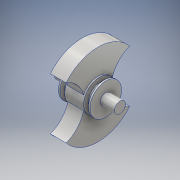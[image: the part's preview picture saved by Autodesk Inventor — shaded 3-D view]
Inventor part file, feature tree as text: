
AUTODESK INVENTOR PART (.ipt)
format: ipt  version: 2016 (Build 200138000, 138)  size: 163,328 bytes
history: native  units: mm
features: sketch x6, extrude x4, revolve x2, other x1
ambient origin geometry x8: Origin, YZ Plane, XZ Plane, XY Plane, X Axis, Y Axis, Z Axis, Center Point
bodies: Body1 (feature_tree)
feature tree (13):
  other  "Sólido1"
  extrude  "Extrusión1"  Depth=38.0mm TaperAngle=0.0deg
  extrude  "Extrusión2"  Depth=10.0mm TaperAngle=0.0deg
  extrude  "Extrusión3"  Depth=12.0mm TaperAngle=0.0deg
  extrude  "Extrusión4"  Depth=20.0mm TaperAngle=0.0deg
  revolve  "Revolución1"  [1 undecoded]
  revolve  "Revolución2"  [1 undecoded]
  sketch  "Boceto1"  dims[d0=7.0mm d1=38.0mm d2=0.0mm]
  sketch  "Boceto2"  dims[d3=44.0mm d6=10.0mm d7=0.0mm]
  sketch  "Boceto3"  dims[d8=20.0mm d9=12.0mm d10=0.0mm]
  sketch  "Boceto4"  dims[d11=14.0mm d12=20.0mm d13=0.0mm]
  sketch  "Boceto6"  dims[d15=1.0mm d16=10.0mm]
  sketch  "Boceto7"  dims[d17=90.0deg d18=1.0mm d19=10.0mm d20=90.0deg d21=52.0mm d22=35.0mm d23=35.0mm]
note: 2 required parameter values undecoded (feature->parameter linkage not recoverable at this tier; creation-order binding heuristic only, values carry confidence <= 0.55)
